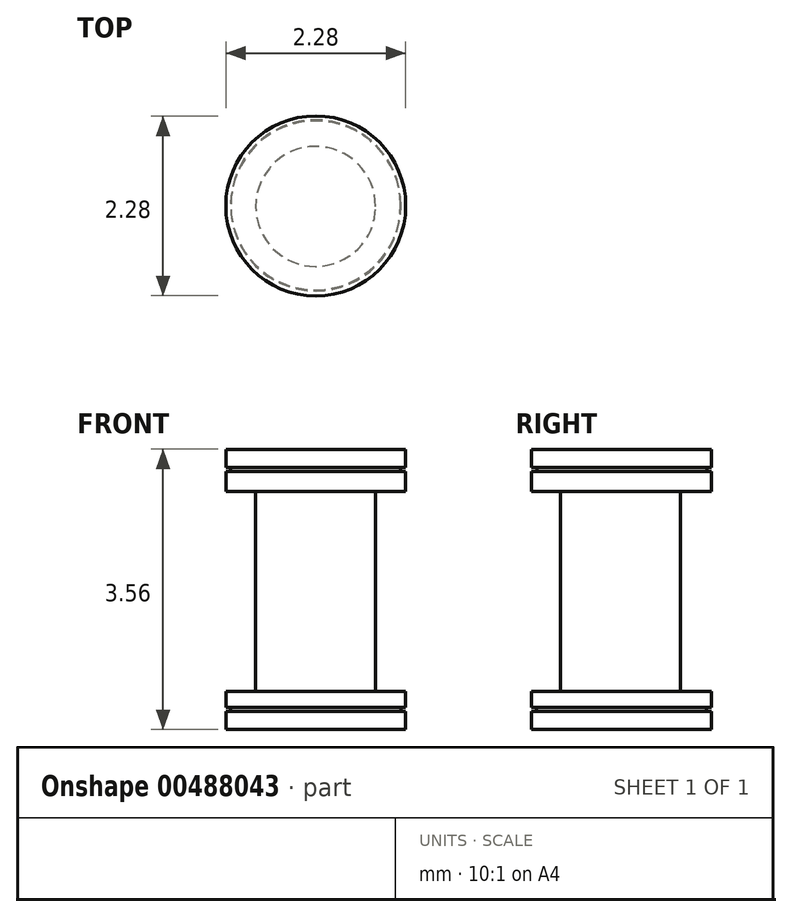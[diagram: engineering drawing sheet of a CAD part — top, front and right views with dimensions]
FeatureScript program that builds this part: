
annotation { "Feature Type Name" : "Feature", "Feature Type Description" : "" }
export const myFeature = defineFeature(function(context is Context, id is Id, definition is map)
    precondition{}
    {
        {
            var Q0;
            Q0=qCreatedBy(makeId("Top.planeOp"),FACE);
            var sketch = newSketch(context, id + "F0", { "sketchPlane" : qUnion([Q0])});
            skCircle(sketch, "E0", {"center": v(0, 0) * mm, "radius": 1.14 * mm});
            skSolve(sketch);
        }
        {
            var Q0;
            Q0=qSketchRegion(id+"F0",true);
            extrude(context, id + "F1", {"entities" : qUnion([Q0]), "depth" : 3.56 * mm, "offsetDistance" : 25.4 * mm});
        }
        {
            var Q0;
            Q0=qCreatedBy(makeId("Top.planeOp"),FACE);
            cPlane(context, id + "F2", {"entities" : qUnion([Q0]), "cplaneType" : CPlaneType.OFFSET, "offset" : 0.23 * mm, "width" : 152.4 * mm, "height" : 152.4 * mm});
        }
        {
            var Q0;
            Q0=qCreatedBy(id+"F2.planeOp",FACE);
            cPlane(context, id + "F3", {"entities" : qUnion([Q0]), "cplaneType" : CPlaneType.OFFSET, "offset" : 3.1 * mm, "width" : 152.4 * mm, "height" : 152.4 * mm});
        }
        {
            var Q0;
            Q0=qCreatedBy(id+"F2.planeOp",FACE);
            var sketch = newSketch(context, id + "F4", { "sketchPlane" : qUnion([Q0])});
            skCircle(sketch, "E1", {"center": v(0, 0) * mm, "radius": 1.08 * mm});
            skCircle(sketch, "E2", {"center": v(0, 0) * mm, "radius": 1.14 * mm});
            skSolve(sketch);
        }
        {
            var Q0;
            Q0=qSketchRegion(id+"F4",true);
            extrude(context, id + "F5", {"entities" : qUnion([Q0]), "operationType" : NewBodyOperationType.REMOVE, "depth" : 0.05 * mm, "offsetDistance" : 25.4 * mm});
        }
        {
            var Q0;
            Q0=qCreatedBy(id+"F3.planeOp",FACE);
            var sketch = newSketch(context, id + "F6", { "sketchPlane" : qUnion([Q0])});
            skCircle(sketch, "E3", {"center": v(0, 0.01) * mm, "radius": 1.08 * mm});
            skCircle(sketch, "E4", {"center": v(0, 0.01) * mm, "radius": 1.16 * mm});
            skSolve(sketch);
        }
        {
            var Q0;
            Q0=qSketchRegion(id+"F6",true);
            var Q1;
            Q1=qConstructionFilter(qBodyType(qCreatedBy(id+"F6",EDGE),BodyType.WIRE),ConstructionObject.NO);
            extrude(context, id + "F7", {"entities" : qUnion([Q0]), "operationType" : NewBodyOperationType.REMOVE, "surfaceEntities" : qUnion([Q1]), "oppositeDirection" : true, "depth" : 0.05 * mm, "offsetDistance" : 25.4 * mm});
        }
        {
            var Q0;
            Q0=qCreatedBy(id+"F2.planeOp",FACE);
            cPlane(context, id + "F8", {"entities" : qUnion([Q0]), "cplaneType" : CPlaneType.OFFSET, "offset" : 0.25 * mm, "width" : 152.4 * mm, "height" : 152.4 * mm});
        }
        {
            var Q0;
            Q0=qCreatedBy(id+"F8.planeOp",FACE);
            var sketch = newSketch(context, id + "F9", { "sketchPlane" : qUnion([Q0])});
            skCircle(sketch, "E5", {"center": v(0, 0) * mm, "radius": 0.76 * mm});
            skCircle(sketch, "E6", {"center": v(0, 0) * mm, "radius": 1.16 * mm});
            skSolve(sketch);
        }
        {
            var Q0;
            Q0=qSketchRegion(id+"F9",true);
            var Q1;
            Q1=qConstructionFilter(qBodyType(qCreatedBy(id+"F9",EDGE),BodyType.WIRE),ConstructionObject.NO);
            extrude(context, id + "F10", {"entities" : qUnion([Q0]), "operationType" : NewBodyOperationType.REMOVE, "surfaceEntities" : qUnion([Q1]), "depth" : 2.54 * mm, "offsetDistance" : 25.4 * mm});
        }
    });
